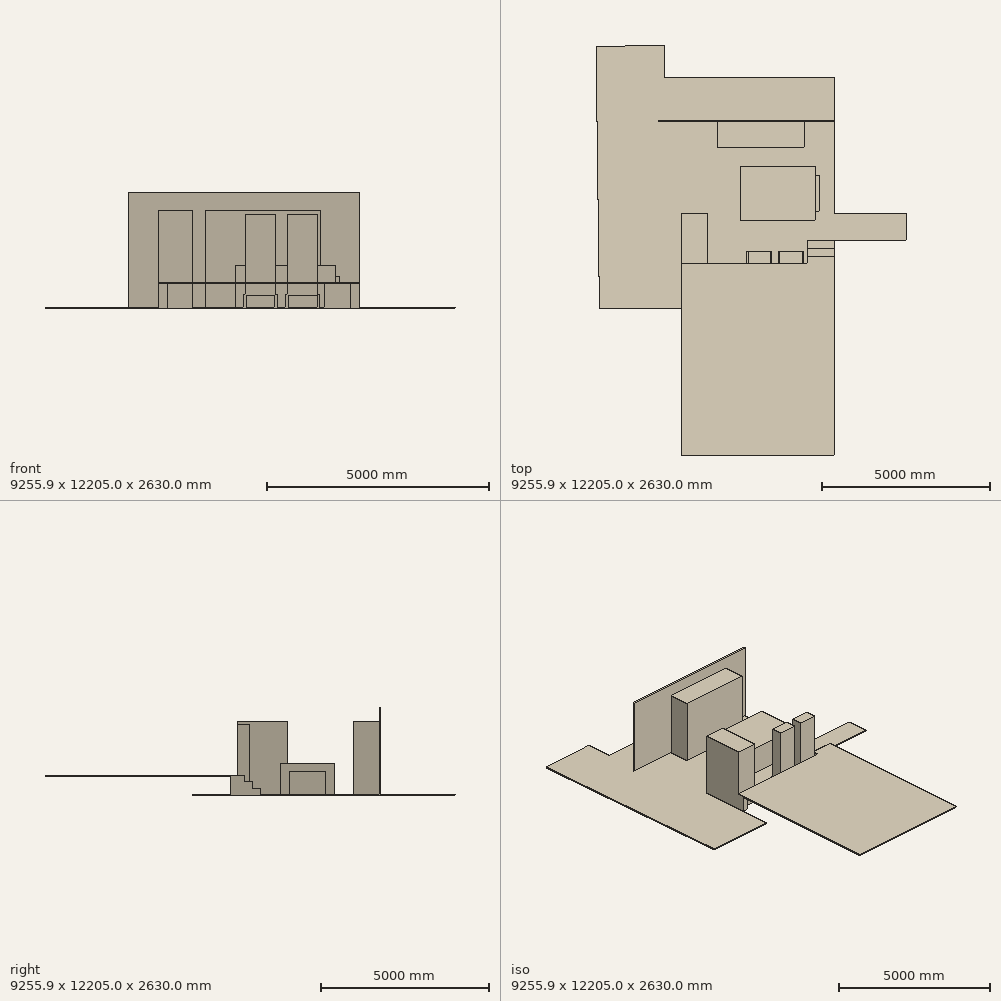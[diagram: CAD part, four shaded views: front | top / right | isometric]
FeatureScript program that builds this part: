
annotation { "Feature Type Name" : "Feature", "Feature Type Description" : "" }
export const myFeature = defineFeature(function(context is Context, id is Id, definition is map)
    precondition{}
    {
        {
            var Q0;
            Q0=qCreatedBy(makeId("Top.planeOp"),FACE);
            var sketch = newSketch(context, id + "F0", { "sketchPlane" : qUnion([Q0])});
            skLineSegment(sketch, "E0.bottom", {"start": v(-1125, 800) * mm, "end": v(1125, 800) * mm});
            skLineSegment(sketch, "E0.top", {"start": v(-1125, -800) * mm, "end": v(1125, -800) * mm});
            skLineSegment(sketch, "E0.left", {"start": v(-1125, 800) * mm, "end": v(-1125, -800) * mm});
            skLineSegment(sketch, "E0.right", {"start": v(1125, 800) * mm, "end": v(1125, -800) * mm});
            skPoint(sketch, "E0.middle", {"position": v(0, 0) * mm});
            skLineSegment(sketch, "E1.bottom", {"start": v(794.97, 2130) * mm, "end": v(-1796.91, 2130) * mm});
            skLineSegment(sketch, "E1.top", {"start": v(794.97, 1380) * mm, "end": v(-1796.91, 1380) * mm});
            skLineSegment(sketch, "E1.left", {"start": v(794.97, 2130) * mm, "end": v(794.97, 1380) * mm});
            skLineSegment(sketch, "E1.right", {"start": v(-1796.91, 2130) * mm, "end": v(-1796.91, 1380) * mm});
            skLineSegment(sketch, "E2", {"start": v(1675, 3460) * mm, "end": v(1675, -610) * mm});
            skLineSegment(sketch, "E3.bottom", {"start": v(766.46, -1730) * mm, "end": v(16.46, -1730) * mm});
            skLineSegment(sketch, "E3.top", {"start": v(766.46, -2100) * mm, "end": v(16.46, -2100) * mm});
            skLineSegment(sketch, "E3.left", {"start": v(766.46, -1730) * mm, "end": v(766.46, -2100) * mm});
            skLineSegment(sketch, "E3.right", {"start": v(16.46, -1730) * mm, "end": v(16.46, -2100) * mm});
            skLineSegment(sketch, "E4.bottom", {"start": v(-183.54, -1730) * mm, "end": v(-933.54, -1730) * mm});
            skLineSegment(sketch, "E4.top", {"start": v(-183.54, -2100) * mm, "end": v(-933.54, -2100) * mm});
            skLineSegment(sketch, "E4.left", {"start": v(-183.54, -1730) * mm, "end": v(-183.54, -2100) * mm});
            skLineSegment(sketch, "E4.right", {"start": v(-933.54, -1730) * mm, "end": v(-933.54, -2100) * mm});
            skLineSegment(sketch, "E5", {"start": v(1675, -610) * mm, "end": v(3053.14, -610) * mm});
            skLineSegment(sketch, "E6", {"start": v(3053.14, -610) * mm, "end": v(3053.14, 361.12) * mm});
            skLineSegment(sketch, "E7", {"start": v(3053.14, 361.12) * mm, "end": v(3843.14, 361.12) * mm});
            skLineSegment(sketch, "E8", {"start": v(3843.14, -1400) * mm, "end": v(2516.8, -1400) * mm});
            skLineSegment(sketch, "E9", {"start": v(2516.8, -1400) * mm, "end": v(2516.8, -3015.82) * mm});
            skLineSegment(sketch, "E10", {"start": v(2516.8, -3015.82) * mm, "end": v(1817.51, -3015.82) * mm});
            skLineSegment(sketch, "E11", {"start": v(1817.51, -3015.82) * mm, "end": v(1817.51, -1400) * mm});
            skLineSegment(sketch, "E12", {"start": v(1817.51, -1400) * mm, "end": v(1675, -1400) * mm});
            skLineSegment(sketch, "E13", {"start": v(1675, -1400) * mm, "end": v(1675, -2100) * mm});
            skLineSegment(sketch, "E14", {"start": v(1675, -2100) * mm, "end": v(885, -2100) * mm});
            skLineSegment(sketch, "E15", {"start": v(885, -2100) * mm, "end": v(885, -1400) * mm});
            skLineSegment(sketch, "E16", {"start": v(885, -2100) * mm, "end": v(-2855, -2100) * mm});
            skLineSegment(sketch, "E17", {"start": v(885, -1400) * mm, "end": v(1675, -1400) * mm});
            skLineSegment(sketch, "E18", {"start": v(1675, -1400) * mm, "end": v(1675, -1400) * mm});
            skLineSegment(sketch, "E19.bottom", {"start": v(-2855, -600) * mm, "end": v(-2105, -600) * mm});
            skLineSegment(sketch, "E19.top", {"start": v(-2855, -2100) * mm, "end": v(-2105, -2100) * mm});
            skLineSegment(sketch, "E19.left", {"start": v(-2855, -600) * mm, "end": v(-2855, -2100) * mm});
            skLineSegment(sketch, "E19.right", {"start": v(-2105, -600) * mm, "end": v(-2105, -2100) * mm});
            skLineSegment(sketch, "E20", {"start": v(2516.8, -1400) * mm, "end": v(1817.51, -1400) * mm});
            skLineSegment(sketch, "E21", {"start": v(3053.14, -610) * mm, "end": v(3843.14, -610) * mm});
            skLineSegment(sketch, "E22", {"start": v(3843.14, 361.12) * mm, "end": v(3843.14, -610) * mm});
            skLineSegment(sketch, "E23", {"start": v(3843.14, -610) * mm, "end": v(3843.14, -1400) * mm});
            skLineSegment(sketch, "E24", {"start": v(-2855, -2100) * mm, "end": v(-2855, -3422.45) * mm});
            skLineSegment(sketch, "E25", {"start": v(-2855, -3422.45) * mm, "end": v(-2855, -7802.65) * mm});
            skLineSegment(sketch, "E26", {"start": v(-2855, -7802.65) * mm, "end": v(1675, -7802.65) * mm});
            skLineSegment(sketch, "E27", {"start": v(1675, -7802.65) * mm, "end": v(1675, -2100) * mm});
            skLineSegment(sketch, "E28", {"start": v(-2855, -3422.45) * mm, "end": v(-5312.24, -3422.45) * mm});
            skLineSegment(sketch, "E29", {"start": v(-5312.24, -3422.45) * mm, "end": v(-5412.78, 4376.25) * mm});
            skLineSegment(sketch, "E30", {"start": v(-5412.78, 4376.25) * mm, "end": v(-3387.29, 4402.36) * mm});
            skLineSegment(sketch, "E31", {"start": v(-3387.29, 4402.36) * mm, "end": v(-3375.14, 3460) * mm});
            skLineSegment(sketch, "E32", {"start": v(-3375.14, 3460) * mm, "end": v(1675, 3460) * mm});
            skLineSegment(sketch, "E33.bottom", {"start": v(-1185.34, -3222.94) * mm, "end": v(110.16, -3222.94) * mm});
            skLineSegment(sketch, "E33.top", {"start": v(-1185.34, -6783.92) * mm, "end": v(110.16, -6783.92) * mm});
            skLineSegment(sketch, "E33.left", {"start": v(-1185.34, -3222.94) * mm, "end": v(-1185.34, -6783.92) * mm});
            skLineSegment(sketch, "E33.right", {"start": v(110.16, -3222.94) * mm, "end": v(110.16, -6783.92) * mm});
            skLineSegment(sketch, "E34.bottom", {"start": v(1675, 2130) * mm, "end": v(-3542.88, 2130) * mm});
            skLineSegment(sketch, "E34.top", {"start": v(1675, 2180) * mm, "end": v(-3542.88, 2180) * mm});
            skLineSegment(sketch, "E34.left", {"start": v(1675, 2130) * mm, "end": v(1675, 2180) * mm});
            skLineSegment(sketch, "E34.right", {"start": v(-3542.88, 2130) * mm, "end": v(-3542.88, 2180) * mm});
            skSolve(sketch);
        }
        {
            var Q0;
            Q0=makeQuery(id+"F0.imprint","IMPRINT",FACE,{"disambiguationData":[TD([[makeQuery(id+"F0.imprint","IMPRINT",EDGE,{"derivedFrom":sQuery(id+"F0.wireOp",EDGE,"E0.bottom")}),-1.0]])]});
            extrude(context, id + "F1", {"entities" : qUnion([Q0]), "depth" : 940 * mm});
        }
        {
            var Q0;
            Q0=qCreatedBy(makeId("Top.planeOp"),FACE);
            var sketch = newSketch(context, id + "F2", { "sketchPlane" : qUnion([Q0])});
            skPoint(sketch, "E35.0", {"position": v(-933.54, -1730) * mm});
            skPoint(sketch, "E36.0", {"position": v(-183.54, -1730) * mm});
            skPoint(sketch, "E37.0", {"position": v(16.46, -1730) * mm});
            skPoint(sketch, "E38.0", {"position": v(766.46, -1730) * mm});
            skPoint(sketch, "E39.0", {"position": v(766.46, -2100) * mm});
            skPoint(sketch, "E40.0", {"position": v(16.46, -2100) * mm});
            skPoint(sketch, "E41.0", {"position": v(-183.54, -2100) * mm});
            skPoint(sketch, "E42.0", {"position": v(-933.54, -2100) * mm});
            skLineSegment(sketch, "E43.bottom", {"start": v(-933.54, -1730) * mm, "end": v(-883.54, -1730) * mm});
            skLineSegment(sketch, "E43.top", {"start": v(-933.54, -1780) * mm, "end": v(-883.54, -1780) * mm});
            skLineSegment(sketch, "E43.left", {"start": v(-933.54, -1730) * mm, "end": v(-933.54, -1780) * mm});
            skLineSegment(sketch, "E43.right", {"start": v(-883.54, -1730) * mm, "end": v(-883.54, -1780) * mm});
            skLineSegment(sketch, "E44.bottom", {"start": v(-933.54, -2100) * mm, "end": v(-883.54, -2100) * mm});
            skLineSegment(sketch, "E44.top", {"start": v(-933.54, -2050) * mm, "end": v(-883.54, -2050) * mm});
            skLineSegment(sketch, "E44.left", {"start": v(-933.54, -2100) * mm, "end": v(-933.54, -2050) * mm});
            skLineSegment(sketch, "E44.right", {"start": v(-883.54, -2100) * mm, "end": v(-883.54, -2050) * mm});
            skLineSegment(sketch, "E45.bottom", {"start": v(-183.54, -2100) * mm, "end": v(-233.54, -2100) * mm});
            skLineSegment(sketch, "E45.top", {"start": v(-183.54, -2050) * mm, "end": v(-233.54, -2050) * mm});
            skLineSegment(sketch, "E45.left", {"start": v(-183.54, -2100) * mm, "end": v(-183.54, -2050) * mm});
            skLineSegment(sketch, "E45.right", {"start": v(-233.54, -2100) * mm, "end": v(-233.54, -2050) * mm});
            skLineSegment(sketch, "E46.bottom", {"start": v(-183.54, -1730) * mm, "end": v(-233.54, -1730) * mm});
            skLineSegment(sketch, "E46.top", {"start": v(-183.54, -1780) * mm, "end": v(-233.54, -1780) * mm});
            skLineSegment(sketch, "E46.left", {"start": v(-183.54, -1730) * mm, "end": v(-183.54, -1780) * mm});
            skLineSegment(sketch, "E46.right", {"start": v(-233.54, -1730) * mm, "end": v(-233.54, -1780) * mm});
            skLineSegment(sketch, "E47.bottom", {"start": v(16.46, -1730) * mm, "end": v(66.46, -1730) * mm});
            skLineSegment(sketch, "E47.top", {"start": v(16.46, -1780) * mm, "end": v(66.46, -1780) * mm});
            skLineSegment(sketch, "E47.left", {"start": v(16.46, -1730) * mm, "end": v(16.46, -1780) * mm});
            skLineSegment(sketch, "E47.right", {"start": v(66.46, -1730) * mm, "end": v(66.46, -1780) * mm});
            skLineSegment(sketch, "E48.bottom", {"start": v(16.46, -2100) * mm, "end": v(66.46, -2100) * mm});
            skLineSegment(sketch, "E48.top", {"start": v(16.46, -2050) * mm, "end": v(66.46, -2050) * mm});
            skLineSegment(sketch, "E48.left", {"start": v(16.46, -2100) * mm, "end": v(16.46, -2050) * mm});
            skLineSegment(sketch, "E48.right", {"start": v(66.46, -2100) * mm, "end": v(66.46, -2050) * mm});
            skLineSegment(sketch, "E49.bottom", {"start": v(766.46, -1730) * mm, "end": v(716.46, -1730) * mm});
            skLineSegment(sketch, "E49.top", {"start": v(766.46, -1780) * mm, "end": v(716.46, -1780) * mm});
            skLineSegment(sketch, "E49.left", {"start": v(766.46, -1730) * mm, "end": v(766.46, -1780) * mm});
            skLineSegment(sketch, "E49.right", {"start": v(716.46, -1730) * mm, "end": v(716.46, -1780) * mm});
            skLineSegment(sketch, "E50.bottom", {"start": v(766.46, -2100) * mm, "end": v(716.46, -2100) * mm});
            skLineSegment(sketch, "E50.top", {"start": v(766.46, -2050) * mm, "end": v(716.46, -2050) * mm});
            skLineSegment(sketch, "E50.left", {"start": v(766.46, -2100) * mm, "end": v(766.46, -2050) * mm});
            skLineSegment(sketch, "E50.right", {"start": v(716.46, -2100) * mm, "end": v(716.46, -2050) * mm});
            skSolve(sketch);
        }
        {
            var Q0;
            Q0 = qSketchRegion(id + "F2", true);
            extrude(context, id + "F3", {"entities" : qUnion([Q0]), "depth" : 300 * mm});
        }
        {
            var Q0;
            Q0=makeQuery(id+"F3.opExtrude","CAP_FACE",FACE,{"disambiguationData":[OSD([sQuery(id+"F2.wireOp",EDGE,"E43.bottom"),sQuery(id+"F2.wireOp",EDGE,"E43.top"),sQuery(id+"F2.wireOp",EDGE,"E43.left"),sQuery(id+"F2.wireOp",EDGE,"E43.right")])],"isStart":false});
            var sketch = newSketch(context, id + "F4", { "sketchPlane" : qUnion([Q0])});
            skLineSegment(sketch, "E51.bottom", {"start": v(-933.54, -1730) * mm, "end": v(-183.54, -1730) * mm});
            skLineSegment(sketch, "E51.top", {"start": v(-933.54, -2100) * mm, "end": v(-183.54, -2100) * mm});
            skLineSegment(sketch, "E51.left", {"start": v(-933.54, -1730) * mm, "end": v(-933.54, -2100) * mm});
            skLineSegment(sketch, "E51.right", {"start": v(-183.54, -1730) * mm, "end": v(-183.54, -2100) * mm});
            skLineSegment(sketch, "E52.bottom", {"start": v(16.46, -1730) * mm, "end": v(766.46, -1730) * mm});
            skLineSegment(sketch, "E52.top", {"start": v(16.46, -2100) * mm, "end": v(766.46, -2100) * mm});
            skLineSegment(sketch, "E52.left", {"start": v(16.46, -1730) * mm, "end": v(16.46, -2100) * mm});
            skLineSegment(sketch, "E52.right", {"start": v(766.46, -1730) * mm, "end": v(766.46, -2100) * mm});
            skSolve(sketch);
        }
        {
            var Q0;
            Q0 = qSketchRegion(id + "F4", true);
            extrude(context, id + "F5", {"entities" : qUnion([Q0]), "operationType" : NewBodyOperationType.ADD, "oppositeDirection" : true, "depth" : 35 * mm});
        }
        {
            var Q0;
            Q0=makeQuery(id+"F0.imprint","IMPRINT",FACE,{"disambiguationData":[TD([[makeQuery(id+"F0.imprint","IMPRINT",EDGE,{"derivedFrom":sQuery(id+"F0.wireOp",EDGE,"E0.bottom")}),1.0]])]});
            var Q1;
            Q1=makeQuery(id+"F0.imprint","IMPRINT",FACE,{"disambiguationData":[TD([[makeQuery(id+"F0.imprint","IMPRINT",EDGE,{"derivedFrom":sQuery(id+"F0.wireOp",EDGE,"E1.top")}),-1.0]])]});
            var Q2;
            Q2=makeQuery(id+"F0.imprint","IMPRINT",FACE,{"disambiguationData":[TD([[makeQuery(id+"F0.imprint","IMPRINT",EDGE,{"derivedFrom":sQuery(id+"F0.wireOp",EDGE,"E19.bottom")}),-1.0]])]});
            var Q3;
            Q3=makeQuery(id+"F0.imprint","IMPRINT",FACE,{"disambiguationData":[TD([[makeQuery(id+"F0.imprint","IMPRINT",EDGE,{"derivedFrom":sQuery(id+"F0.wireOp",EDGE,"E13")}),-1.0]])]});
            var Q4;
            Q4=makeQuery(id+"F0.imprint","IMPRINT",FACE,{"disambiguationData":[TD([[makeQuery(id+"F0.imprint","IMPRINT",EDGE,{"derivedFrom":sQuery(id+"F0.wireOp",EDGE,"E4.bottom")}),1.0]])]});
            var Q5;
            Q5=makeQuery(id+"F0.imprint","IMPRINT",FACE,{"disambiguationData":[TD([[makeQuery(id+"F0.imprint","IMPRINT",EDGE,{"derivedFrom":sQuery(id+"F0.wireOp",EDGE,"E3.bottom")}),1.0]])]});
            var Q6;
            Q6=makeQuery(id+"F0.imprint","IMPRINT",FACE,{"disambiguationData":[TD([[makeQuery(id+"F0.imprint","IMPRINT",EDGE,{"derivedFrom":sQuery(id+"F0.wireOp",EDGE,"E34.top")}),1.0]])]});
            var Q7;
            Q7=makeQuery(id+"F0.imprint","IMPRINT",FACE,{"disambiguationData":[TD([[makeQuery(id+"F0.imprint","IMPRINT",EDGE,{"derivedFrom":sQuery(id+"F0.wireOp",EDGE,"E0.bottom")}),-1.0]])]});
            extrude(context, id + "F6", {"entities" : qUnion([Q0, Q1, Q2, Q3, Q4, Q5, Q6, Q7]), "operationType" : NewBodyOperationType.ADD, "oppositeDirection" : true, "depth" : 30 * mm});
        }
        {
            var Q0;
            Q0=makeQuery(id+"F5.boolean.opBoolean","MERGE",FACE,{"derivedFrom":[makeQuery(id+"F3.opExtrude","CAP_FACE",FACE,{"disambiguationData":[OSD([sQuery(id+"F2.wireOp",EDGE,"E43.bottom"),sQuery(id+"F2.wireOp",EDGE,"E43.top"),sQuery(id+"F2.wireOp",EDGE,"E43.left"),sQuery(id+"F2.wireOp",EDGE,"E43.right")])],"isStart":false}),makeQuery(id+"F3.opExtrude","CAP_FACE",FACE,{"disambiguationData":[OSD([sQuery(id+"F2.wireOp",EDGE,"E44.bottom"),sQuery(id+"F2.wireOp",EDGE,"E44.top"),sQuery(id+"F2.wireOp",EDGE,"E44.left"),sQuery(id+"F2.wireOp",EDGE,"E44.right")])],"isStart":false}),makeQuery(id+"F3.opExtrude","CAP_FACE",FACE,{"disambiguationData":[OSD([sQuery(id+"F2.wireOp",EDGE,"E45.bottom"),sQuery(id+"F2.wireOp",EDGE,"E45.top"),sQuery(id+"F2.wireOp",EDGE,"E45.left"),sQuery(id+"F2.wireOp",EDGE,"E45.right")])],"isStart":false}),makeQuery(id+"F3.opExtrude","CAP_FACE",FACE,{"disambiguationData":[OSD([sQuery(id+"F2.wireOp",EDGE,"E46.bottom"),sQuery(id+"F2.wireOp",EDGE,"E46.top"),sQuery(id+"F2.wireOp",EDGE,"E46.left"),sQuery(id+"F2.wireOp",EDGE,"E46.right")])],"isStart":false}),makeQuery(id+"F5.opExtrude","CAP_FACE",FACE,{"disambiguationData":[OSD([sQuery(id+"F4.wireOp",EDGE,"E51.bottom"),sQuery(id+"F4.wireOp",EDGE,"E51.top"),sQuery(id+"F4.wireOp",EDGE,"E51.left"),sQuery(id+"F4.wireOp",EDGE,"E51.right")])],"isStart":true})]});
            var sketch = newSketch(context, id + "F7", { "sketchPlane" : qUnion([Q0])});
            skLineSegment(sketch, "E53.bottom", {"start": v(-888.54, -1730) * mm, "end": v(-228.54, -1730) * mm});
            skLineSegment(sketch, "E53.top", {"start": v(-888.54, -2100) * mm, "end": v(-228.54, -2100) * mm});
            skLineSegment(sketch, "E53.left", {"start": v(-888.54, -1730) * mm, "end": v(-888.54, -2100) * mm});
            skLineSegment(sketch, "E53.right", {"start": v(-228.54, -1730) * mm, "end": v(-228.54, -2100) * mm});
            skPoint(sketch, "E53.middle", {"position": v(-558.54, -1915) * mm});
            skLineSegment(sketch, "E54.bottom", {"start": v(61.46, -1730) * mm, "end": v(721.46, -1730) * mm});
            skLineSegment(sketch, "E54.top", {"start": v(61.46, -2100) * mm, "end": v(721.46, -2100) * mm});
            skLineSegment(sketch, "E54.left", {"start": v(61.46, -1730) * mm, "end": v(61.46, -2100) * mm});
            skLineSegment(sketch, "E54.right", {"start": v(721.46, -1730) * mm, "end": v(721.46, -2100) * mm});
            skPoint(sketch, "E54.middle", {"position": v(391.46, -1915) * mm});
            skLineSegment(sketch, "E55", {"start": v(-558.54, -1730) * mm, "end": v(-558.54, -2100) * mm, "construction": true});
            skSolve(sketch);
        }
        {
            var Q0;
            Q0 = qSketchRegion(id + "F7", true);
            extrude(context, id + "F8", {"entities" : qUnion([Q0]), "operationType" : NewBodyOperationType.ADD, "depth" : 1800 * mm});
        }
        {
            var Q0;
            Q0=makeQuery(id+"F1.opExtrude","SWEPT_FACE",FACE,{"disambiguationData":[OSD([sQuery(id+"F0.wireOp",EDGE,"E0.right")])]});
            var sketch = newSketch(context, id + "F9", { "sketchPlane" : qUnion([Q0])});
            skLineSegment(sketch, "E56.bottom", {"start": v(-525, 0) * mm, "end": v(525, 0) * mm});
            skLineSegment(sketch, "E56.top", {"start": v(-525, 690) * mm, "end": v(525, 690) * mm});
            skLineSegment(sketch, "E56.left", {"start": v(-525, 0) * mm, "end": v(-525, 690) * mm});
            skLineSegment(sketch, "E56.right", {"start": v(525, 0) * mm, "end": v(525, 690) * mm});
            skPoint(sketch, "E57", {"position": v(0, 690) * mm});
            skSolve(sketch);
        }
        {
            var Q0;
            Q0 = qSketchRegion(id + "F9", true);
            extrude(context, id + "F10", {"entities" : qUnion([Q0]), "operationType" : NewBodyOperationType.ADD, "depth" : 100 * mm});
        }
        {
            var Q0;
            Q0=makeQuery(id+"F0.imprint","IMPRINT",FACE,{"disambiguationData":[TD([[makeQuery(id+"F0.imprint","IMPRINT",EDGE,{"derivedFrom":sQuery(id+"F0.wireOp",EDGE,"E1.top")}),-1.0]])]});
            extrude(context, id + "F11", {"entities" : qUnion([Q0]), "operationType" : NewBodyOperationType.ADD, "depth" : 2180 * mm});
        }
        {
            var Q0;
            Q0=makeQuery(id+"F0.imprint","IMPRINT",FACE,{"disambiguationData":[TD([[makeQuery(id+"F0.imprint","IMPRINT",EDGE,{"derivedFrom":sQuery(id+"F0.wireOp",EDGE,"E34.top")}),1.0]])]});
            extrude(context, id + "F12", {"entities" : qUnion([Q0]), "operationType" : NewBodyOperationType.ADD, "depth" : 2600 * mm});
        }
        {
            var Q0;
            Q0=makeQuery(id+"F0.imprint","IMPRINT",FACE,{"disambiguationData":[TD([[makeQuery(id+"F0.imprint","IMPRINT",EDGE,{"derivedFrom":sQuery(id+"F0.wireOp",EDGE,"E19.bottom")}),-1.0]])]});
            var Q1;
            Q1=makeQuery(id+"F11.opExtrude","CAP_FACE",FACE,{"disambiguationData":[OSD([sQuery(id+"F0.wireOp",EDGE,"E1.top"),sQuery(id+"F0.wireOp",EDGE,"E1.left"),sQuery(id+"F0.wireOp",EDGE,"E1.right"),sQuery(id+"F0.wireOp",EDGE,"E34.bottom")])],"isStart":false});
            extrude(context, id + "F13", {"entities" : qUnion([Q0]), "operationType" : NewBodyOperationType.ADD, "endBound" : BoundingType.UP_TO_SURFACE, "endBoundEntityFace" : qUnion([Q1]), "depth" : 2110 * mm});
        }
        {
            var Q0;
            Q0=makeQuery(id+"F6.opExtrude","CAP_FACE",FACE,{"disambiguationData":[OSD([sQuery(id+"F0.wireOp",EDGE,"E2"),sQuery(id+"F0.wireOp",EDGE,"E5"),sQuery(id+"F0.wireOp",EDGE,"E8"),sQuery(id+"F0.wireOp",EDGE,"E12"),sQuery(id+"F0.wireOp",EDGE,"E13"),sQuery(id+"F0.wireOp",EDGE,"E14"),sQuery(id+"F0.wireOp",EDGE,"E16"),sQuery(id+"F0.wireOp",EDGE,"E19.top"),sQuery(id+"F0.wireOp",EDGE,"E20"),sQuery(id+"F0.wireOp",EDGE,"E21"),sQuery(id+"F0.wireOp",EDGE,"E23"),sQuery(id+"F0.wireOp",EDGE,"E24"),sQuery(id+"F0.wireOp",EDGE,"E28"),sQuery(id+"F0.wireOp",EDGE,"E29"),sQuery(id+"F0.wireOp",EDGE,"E30"),sQuery(id+"F0.wireOp",EDGE,"E31"),sQuery(id+"F0.wireOp",EDGE,"E32"),sQuery(id+"F0.wireOp",EDGE,"E34.left")])],"isStart":false});
            var sketch = newSketch(context, id + "F14", { "sketchPlane" : qUnion([Q0])});
            skLineSegment(sketch, "E58.bottom", {"start": v(-2855, 2100) * mm, "end": v(-2655, 2100) * mm});
            skLineSegment(sketch, "E58.top", {"start": v(-2855, 2300) * mm, "end": v(-2655, 2300) * mm});
            skLineSegment(sketch, "E58.left", {"start": v(-2855, 2100) * mm, "end": v(-2855, 2300) * mm});
            skLineSegment(sketch, "E58.right", {"start": v(-2655, 2100) * mm, "end": v(-2655, 2300) * mm});
            skLineSegment(sketch, "E59.bottom", {"start": v(1675, 2100) * mm, "end": v(1475, 2100) * mm});
            skLineSegment(sketch, "E59.top", {"start": v(1675, 2300) * mm, "end": v(1475, 2300) * mm});
            skLineSegment(sketch, "E59.left", {"start": v(1675, 2100) * mm, "end": v(1675, 2300) * mm});
            skLineSegment(sketch, "E59.right", {"start": v(1475, 2100) * mm, "end": v(1475, 2300) * mm});
            skSolve(sketch);
        }
        {
            var Q0;
            Q0 = qSketchRegion(id + "F14", true);
            extrude(context, id + "F15", {"entities" : qUnion([Q0]), "operationType" : NewBodyOperationType.ADD, "oppositeDirection" : true, "depth" : 600 * mm});
        }
        {
            var Q0;
            Q0=makeQuery(id+"F15.opExtrude","CAP_FACE",FACE,{"disambiguationData":[OSD([sQuery(id+"F14.wireOp",EDGE,"E58.bottom"),sQuery(id+"F14.wireOp",EDGE,"E58.top"),sQuery(id+"F14.wireOp",EDGE,"E58.left"),sQuery(id+"F14.wireOp",EDGE,"E58.right")])],"isStart":false});
            var sketch = newSketch(context, id + "F16", { "sketchPlane" : qUnion([Q0])});
            skLineSegment(sketch, "E60.0.0", {"start": v(1675, -7802.65) * mm, "end": v(1675, -2100) * mm});
            skLineSegment(sketch, "E60.0.1", {"start": v(1675, -2100) * mm, "end": v(885, -2100) * mm});
            skLineSegment(sketch, "E60.0.2", {"start": v(885, -2100) * mm, "end": v(766.46, -2100) * mm});
            skLineSegment(sketch, "E60.0.3", {"start": v(766.46, -2100) * mm, "end": v(16.46, -2100) * mm});
            skLineSegment(sketch, "E60.0.4", {"start": v(16.46, -2100) * mm, "end": v(-183.54, -2100) * mm});
            skLineSegment(sketch, "E60.0.5", {"start": v(-183.54, -2100) * mm, "end": v(-933.54, -2100) * mm});
            skLineSegment(sketch, "E60.0.6", {"start": v(-933.54, -2100) * mm, "end": v(-2105, -2100) * mm});
            skLineSegment(sketch, "E60.0.7", {"start": v(-2105, -2100) * mm, "end": v(-2855, -2100) * mm});
            skLineSegment(sketch, "E60.0.8", {"start": v(-2855, -2100) * mm, "end": v(-2855, -3422.45) * mm});
            skLineSegment(sketch, "E60.0.9", {"start": v(-2855, -3422.45) * mm, "end": v(-2855, -7802.65) * mm});
            skLineSegment(sketch, "E60.0.10", {"start": v(-2855, -7802.65) * mm, "end": v(1675, -7802.65) * mm});
            skSolve(sketch);
        }
        {
            var Q0;
            Q0 = qSketchRegion(id + "F16", true);
            extrude(context, id + "F17", {"entities" : qUnion([Q0]), "operationType" : NewBodyOperationType.ADD, "oppositeDirection" : true, "depth" : 30 * mm});
        }
        {
            var Q0;
            Q0=makeQuery(id+"F17.boolean.opBoolean","MERGE",FACE,{"derivedFrom":[makeQuery(id+"F15.boolean.opBoolean","MERGE",FACE,{"derivedFrom":[makeQuery(id+"F6.opExtrude","SWEPT_FACE",FACE,{"disambiguationData":[OSD([sQuery(id+"F0.wireOp",EDGE,"E13")])]}),makeQuery(id+"F15.opExtrude","SWEPT_FACE",FACE,{"disambiguationData":[OSD([sQuery(id+"F14.wireOp",EDGE,"E59.left")])]})]}),makeQuery(id+"F17.opExtrude","SWEPT_FACE",FACE,{"disambiguationData":[OSD([sQuery(id+"F16.wireOp",EDGE,"E60.0.0")])]})]});
            var sketch = newSketch(context, id + "F18", { "sketchPlane" : qUnion([Q0])});
            skLineSegment(sketch, "E61", {"start": v(-2100, 570) * mm, "end": v(-1866.67, 570) * mm});
            skLineSegment(sketch, "E62", {"start": v(-1866.67, 570) * mm, "end": v(-1866.67, 380) * mm});
            skLineSegment(sketch, "E63", {"start": v(-1866.67, 380) * mm, "end": v(-1633.33, 380) * mm});
            skLineSegment(sketch, "E64", {"start": v(-1633.33, 380) * mm, "end": v(-1633.33, 190) * mm});
            skLineSegment(sketch, "E65", {"start": v(-1633.33, 190) * mm, "end": v(-1400, 190) * mm});
            skLineSegment(sketch, "E66", {"start": v(-1400, 190) * mm, "end": v(-1400, 0) * mm});
            skLineSegment(sketch, "E67", {"start": v(-1400, 0) * mm, "end": v(-2100, 0) * mm});
            skLineSegment(sketch, "E68", {"start": v(-2100, 0) * mm, "end": v(-2100, 570) * mm});
            skSolve(sketch);
        }
        {
            var Q0;
            Q0 = qSketchRegion(id + "F18", true);
            var Q1;
            Q1=sQuery(id+"F0.wireOp",VERTEX,"E15.end");
            extrude(context, id + "F19", {"entities" : qUnion([Q0]), "operationType" : NewBodyOperationType.ADD, "endBound" : BoundingType.UP_TO_VERTEX, "oppositeDirection" : true, "endBoundEntityVertex" : qUnion([Q1]), "depth" : 25 * mm});
        }
    });
